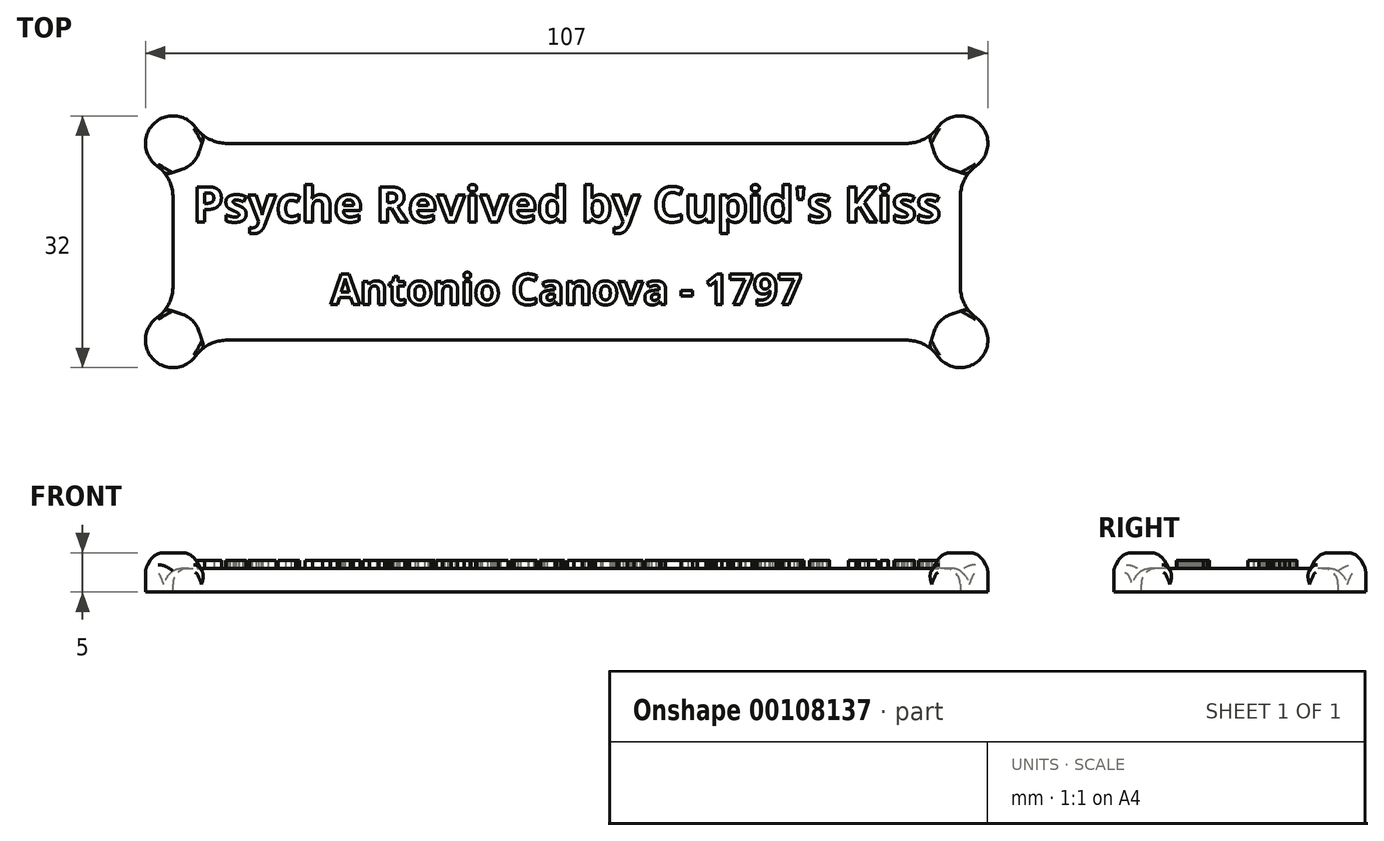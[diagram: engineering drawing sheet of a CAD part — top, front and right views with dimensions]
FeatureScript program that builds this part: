
annotation { "Feature Type Name" : "Feature", "Feature Type Description" : "" }
export const myFeature = defineFeature(function(context is Context, id is Id, definition is map)
    precondition{}
    {
        {
            var Q0;
            Q0=qCreatedBy(makeId("Top.planeOp"),FACE);
            var sketch = newSketch(context, id + "F0", { "sketchPlane" : qUnion([Q0])});
            skLineSegment(sketch, "E0.bottom", {"start": v(50, -12.5) * mm, "end": v(-50, -12.5) * mm});
            skLineSegment(sketch, "E0.top", {"start": v(50, 12.5) * mm, "end": v(-50, 12.5) * mm});
            skLineSegment(sketch, "E0.left", {"start": v(50, -12.5) * mm, "end": v(50, 12.5) * mm});
            skLineSegment(sketch, "E0.right", {"start": v(-50, -12.5) * mm, "end": v(-50, 12.5) * mm});
            skPoint(sketch, "E0.middle", {"position": v(0, 0) * mm});
            skArc(sketch, "E1", {"start": v(-46.5, 12.5) * mm, "mid": v(-52.47, 14.97) * mm, "end": v(-50, 9) * mm});
            skCircle(sketch, "E2", {"center": v(-50, -12.5) * mm, "radius": 3.5 * mm});
            skCircle(sketch, "E3", {"center": v(50, -12.5) * mm, "radius": 3.5 * mm});
            skCircle(sketch, "E4", {"center": v(50, 12.5) * mm, "radius": 3.5 * mm});
            skCircle(sketch, "E5", {"center": v(-50, 12.5) * mm, "radius": 3.5 * mm});
            skSolve(sketch);
        }
        {
            var Q0;
            {var subQ0=sQuery(id+"F0.wireOp",EDGE,"E0.left");var subQ1=sQuery(id+"F0.wireOp",EDGE,"E0.bottom");var subQ2=makeQuery(id+"F0.imprint","INTERSECT",VERTEX,{"derivedFrom":[subQ1,subQ0]});Q0=makeQuery(id+"F0.imprint","IMPRINT",FACE,{"disambiguationData":[TD([[makeQuery(id+"F0.imprint","IMPRINT",EDGE,{"disambiguationData":[TD([[subQ2,-1.0]])],"derivedFrom":subQ1}),1.0]])]});}
            var Q1;
            {var subQ0=sQuery(id+"F0.wireOp",EDGE,"E0.right");var subQ1=sQuery(id+"F0.wireOp",EDGE,"E0.bottom");var subQ2=makeQuery(id+"F0.imprint","INTERSECT",VERTEX,{"derivedFrom":[subQ1,subQ0]});Q1=makeQuery(id+"F0.imprint","IMPRINT",FACE,{"disambiguationData":[TD([[makeQuery(id+"F0.imprint","IMPRINT",EDGE,{"disambiguationData":[TD([[subQ2,1.0]])],"derivedFrom":subQ1}),1.0]])]});}
            var Q2;
            {var subQ0=sQuery(id+"F0.wireOp",EDGE,"E0.left");var subQ1=sQuery(id+"F0.wireOp",EDGE,"E0.top");var subQ2=makeQuery(id+"F0.imprint","INTERSECT",VERTEX,{"derivedFrom":[subQ1,subQ0]});Q2=makeQuery(id+"F0.imprint","IMPRINT",FACE,{"disambiguationData":[TD([[makeQuery(id+"F0.imprint","IMPRINT",EDGE,{"disambiguationData":[TD([[subQ2,-1.0]])],"derivedFrom":subQ1}),-1.0]])]});}
            var Q3;
            {var subQ3=sQuery(id+"F0.wireOp",EDGE,"E1");Q3=makeQuery(id+"F0.imprint","IMPRINT",FACE,{"disambiguationData":[TD([[makeQuery(id+"F0.imprint","IMPRINT",EDGE,{"derivedFrom":subQ3}),1.0]])]});}
            var Q4;
            {var subQ0=sQuery(id+"F0.wireOp",EDGE,"E0.left");var subQ1=sQuery(id+"F0.wireOp",EDGE,"E0.bottom");var subQ2=makeQuery(id+"F0.imprint","INTERSECT",VERTEX,{"derivedFrom":[subQ1,subQ0]});Q4=makeQuery(id+"F0.imprint","IMPRINT",FACE,{"disambiguationData":[TD([[makeQuery(id+"F0.imprint","IMPRINT",EDGE,{"disambiguationData":[TD([[subQ2,-1.0]])],"derivedFrom":subQ1}),-1.0]])]});}
            var Q5;
            {var subQ0=sQuery(id+"F0.wireOp",EDGE,"E0.right");var subQ1=sQuery(id+"F0.wireOp",EDGE,"E0.bottom");var subQ2=makeQuery(id+"F0.imprint","INTERSECT",VERTEX,{"derivedFrom":[subQ1,subQ0]});Q5=makeQuery(id+"F0.imprint","IMPRINT",FACE,{"disambiguationData":[TD([[makeQuery(id+"F0.imprint","IMPRINT",EDGE,{"disambiguationData":[TD([[subQ2,1.0]])],"derivedFrom":subQ1}),-1.0]])]});}
            var Q6;
            {var subQ0=sQuery(id+"F0.wireOp",EDGE,"E0.left");var subQ1=sQuery(id+"F0.wireOp",EDGE,"E0.top");var subQ2=makeQuery(id+"F0.imprint","INTERSECT",VERTEX,{"derivedFrom":[subQ1,subQ0]});Q6=makeQuery(id+"F0.imprint","IMPRINT",FACE,{"disambiguationData":[TD([[makeQuery(id+"F0.imprint","IMPRINT",EDGE,{"disambiguationData":[TD([[subQ2,-1.0]])],"derivedFrom":subQ1}),1.0]])]});}
            var Q7;
            Q7=makeQuery(id+"F0.imprint","IMPRINT",FACE,{"disambiguationData":[TD([[makeQuery(id+"F0.imprint","IMPRINT",EDGE,{"derivedFrom":sQuery(id+"F0.wireOp",EDGE,"687687a7-fea7-4981-826e-90962389b271.sketch_text.stroke-0")}),1.0]])]});
            var Q8;
            Q8 = qSketchRegion(id + "F0", true);
            var Q9;
            Q9=makeQuery(id+"F0.imprint","IMPRINT",FACE,{"disambiguationData":[TD([[makeQuery(id+"F0.imprint","IMPRINT",EDGE,{"derivedFrom":sQuery(id+"F0.wireOp",EDGE,"687687a7-fea7-4981-826e-90962389b271.sketch_text.stroke-211")}),1.0]])]});
            var Q10;
            Q10=makeQuery(id+"F0.imprint","IMPRINT",FACE,{"disambiguationData":[TD([[makeQuery(id+"F0.imprint","IMPRINT",EDGE,{"derivedFrom":sQuery(id+"F0.wireOp",EDGE,"1d88de1f-9107-434d-85d9-702cc254aeca.sketch_text.stroke-49")}),-1.0]])]});
            var Q11;
            Q11=makeQuery(id+"F0.imprint","IMPRINT",FACE,{"disambiguationData":[TD([[makeQuery(id+"F0.imprint","IMPRINT",EDGE,{"derivedFrom":sQuery(id+"F0.wireOp",EDGE,"1d88de1f-9107-434d-85d9-702cc254aeca.sketch_text.stroke-238")}),-1.0]])]});
            var Q12;
            Q12=makeQuery(id+"F0.imprint","IMPRINT",FACE,{"disambiguationData":[TD([[makeQuery(id+"F0.imprint","IMPRINT",EDGE,{"derivedFrom":sQuery(id+"F0.wireOp",EDGE,"1d88de1f-9107-434d-85d9-702cc254aeca.sketch_text.stroke-8")}),1.0]])]});
            var Q13;
            Q13=makeQuery(id+"F0.imprint","IMPRINT",FACE,{"disambiguationData":[TD([[makeQuery(id+"F0.imprint","IMPRINT",EDGE,{"derivedFrom":sQuery(id+"F0.wireOp",EDGE,"687687a7-fea7-4981-826e-90962389b271.sketch_text.stroke-235")}),1.0]])]});
            var Q14;
            Q14=makeQuery(id+"F0.imprint","IMPRINT",FACE,{"disambiguationData":[TD([[makeQuery(id+"F0.imprint","IMPRINT",EDGE,{"derivedFrom":sQuery(id+"F0.wireOp",EDGE,"1d88de1f-9107-434d-85d9-702cc254aeca.sketch_text.stroke-95")}),-1.0]])]});
            var Q15;
            Q15=makeQuery(id+"F0.imprint","IMPRINT",FACE,{"disambiguationData":[TD([[makeQuery(id+"F0.imprint","IMPRINT",EDGE,{"derivedFrom":sQuery(id+"F0.wireOp",EDGE,"1d88de1f-9107-434d-85d9-702cc254aeca.sketch_text.stroke-261")}),1.0]])]});
            var Q16;
            Q16=makeQuery(id+"F0.imprint","IMPRINT",FACE,{"disambiguationData":[TD([[makeQuery(id+"F0.imprint","IMPRINT",EDGE,{"derivedFrom":sQuery(id+"F0.wireOp",EDGE,"1d88de1f-9107-434d-85d9-702cc254aeca.sketch_text.stroke-13")}),-1.0]])]});
            var Q17;
            Q17=makeQuery(id+"F0.imprint","IMPRINT",FACE,{"disambiguationData":[TD([[makeQuery(id+"F0.imprint","IMPRINT",EDGE,{"derivedFrom":sQuery(id+"F0.wireOp",EDGE,"687687a7-fea7-4981-826e-90962389b271.sketch_text.stroke-243")}),-1.0]])]});
            var Q18;
            Q18=makeQuery(id+"F0.imprint","IMPRINT",FACE,{"disambiguationData":[TD([[makeQuery(id+"F0.imprint","IMPRINT",EDGE,{"derivedFrom":sQuery(id+"F0.wireOp",EDGE,"1d88de1f-9107-434d-85d9-702cc254aeca.sketch_text.stroke-127")}),-1.0]])]});
            var Q19;
            Q19=makeQuery(id+"F0.imprint","IMPRINT",FACE,{"disambiguationData":[TD([[makeQuery(id+"F0.imprint","IMPRINT",EDGE,{"derivedFrom":sQuery(id+"F0.wireOp",EDGE,"1d88de1f-9107-434d-85d9-702cc254aeca.sketch_text.stroke-271")}),-1.0]])]});
            var Q20;
            Q20=makeQuery(id+"F0.imprint","IMPRINT",FACE,{"disambiguationData":[TD([[makeQuery(id+"F0.imprint","IMPRINT",EDGE,{"derivedFrom":sQuery(id+"F0.wireOp",EDGE,"1d88de1f-9107-434d-85d9-702cc254aeca.sketch_text.stroke-30")}),-1.0]])]});
            var Q21;
            Q21=makeQuery(id+"F0.imprint","IMPRINT",FACE,{"disambiguationData":[TD([[makeQuery(id+"F0.imprint","IMPRINT",EDGE,{"derivedFrom":sQuery(id+"F0.wireOp",EDGE,"687687a7-fea7-4981-826e-90962389b271.sketch_text.stroke-259")}),-1.0]])]});
            var Q22;
            Q22=makeQuery(id+"F0.imprint","IMPRINT",FACE,{"disambiguationData":[TD([[makeQuery(id+"F0.imprint","IMPRINT",EDGE,{"derivedFrom":sQuery(id+"F0.wireOp",EDGE,"1d88de1f-9107-434d-85d9-702cc254aeca.sketch_text.stroke-171")}),-1.0]])]});
            var Q23;
            Q23=makeQuery(id+"F0.imprint","IMPRINT",FACE,{"disambiguationData":[TD([[makeQuery(id+"F0.imprint","IMPRINT",EDGE,{"derivedFrom":sQuery(id+"F0.wireOp",EDGE,"1d88de1f-9107-434d-85d9-702cc254aeca.sketch_text.stroke-58")}),1.0]])]});
            var Q24;
            Q24=makeQuery(id+"F0.imprint","IMPRINT",FACE,{"disambiguationData":[TD([[makeQuery(id+"F0.imprint","IMPRINT",EDGE,{"derivedFrom":sQuery(id+"F0.wireOp",EDGE,"687687a7-fea7-4981-826e-90962389b271.sketch_text.stroke-274")}),-1.0]])]});
            var Q25;
            Q25=makeQuery(id+"F0.imprint","IMPRINT",FACE,{"disambiguationData":[TD([[makeQuery(id+"F0.imprint","IMPRINT",EDGE,{"derivedFrom":sQuery(id+"F0.wireOp",EDGE,"1d88de1f-9107-434d-85d9-702cc254aeca.sketch_text.stroke-198")}),-1.0]])]});
            var Q26;
            Q26=makeQuery(id+"F0.imprint","IMPRINT",FACE,{"disambiguationData":[TD([[makeQuery(id+"F0.imprint","IMPRINT",EDGE,{"derivedFrom":sQuery(id+"F0.wireOp",EDGE,"1d88de1f-9107-434d-85d9-702cc254aeca.sketch_text.stroke-66")}),-1.0]])]});
            var Q27;
            Q27=makeQuery(id+"F0.imprint","IMPRINT",FACE,{"disambiguationData":[TD([[makeQuery(id+"F0.imprint","IMPRINT",EDGE,{"derivedFrom":sQuery(id+"F0.wireOp",EDGE,"1d88de1f-9107-434d-85d9-702cc254aeca.sketch_text.stroke-245")}),-1.0]])]});
            var Q28;
            Q28=makeQuery(id+"F0.imprint","IMPRINT",FACE,{"disambiguationData":[TD([[makeQuery(id+"F0.imprint","IMPRINT",EDGE,{"derivedFrom":sQuery(id+"F0.wireOp",EDGE,"1d88de1f-9107-434d-85d9-702cc254aeca.sketch_text.stroke-83")}),-1.0]])]});
            var Q29;
            Q29=makeQuery(id+"F0.imprint","IMPRINT",FACE,{"disambiguationData":[TD([[makeQuery(id+"F0.imprint","IMPRINT",EDGE,{"derivedFrom":sQuery(id+"F0.wireOp",EDGE,"687687a7-fea7-4981-826e-90962389b271.sketch_text.stroke-307")}),1.0]])]});
            var Q30;
            Q30=makeQuery(id+"F0.imprint","IMPRINT",FACE,{"disambiguationData":[TD([[makeQuery(id+"F0.imprint","IMPRINT",EDGE,{"derivedFrom":sQuery(id+"F0.wireOp",EDGE,"687687a7-fea7-4981-826e-90962389b271.sketch_text.stroke-0")}),-1.0]])]});
            var Q31;
            Q31=makeQuery(id+"F0.imprint","IMPRINT",FACE,{"disambiguationData":[TD([[makeQuery(id+"F0.imprint","IMPRINT",EDGE,{"derivedFrom":sQuery(id+"F0.wireOp",EDGE,"1d88de1f-9107-434d-85d9-702cc254aeca.sketch_text.stroke-87")}),-1.0]])]});
            var Q32;
            Q32=makeQuery(id+"F0.imprint","IMPRINT",FACE,{"disambiguationData":[TD([[makeQuery(id+"F0.imprint","IMPRINT",EDGE,{"derivedFrom":sQuery(id+"F0.wireOp",EDGE,"687687a7-fea7-4981-826e-90962389b271.sketch_text.stroke-316")}),-1.0]])]});
            var Q33;
            Q33=makeQuery(id+"F0.imprint","IMPRINT",FACE,{"disambiguationData":[TD([[makeQuery(id+"F0.imprint","IMPRINT",EDGE,{"derivedFrom":sQuery(id+"F0.wireOp",EDGE,"687687a7-fea7-4981-826e-90962389b271.sketch_text.stroke-119")}),1.0]])]});
            var Q34;
            Q34=makeQuery(id+"F0.imprint","IMPRINT",FACE,{"disambiguationData":[TD([[makeQuery(id+"F0.imprint","IMPRINT",EDGE,{"derivedFrom":sQuery(id+"F0.wireOp",EDGE,"687687a7-fea7-4981-826e-90962389b271.sketch_text.stroke-89")}),-1.0]])]});
            var Q35;
            Q35=makeQuery(id+"F0.imprint","IMPRINT",FACE,{"disambiguationData":[TD([[makeQuery(id+"F0.imprint","IMPRINT",EDGE,{"derivedFrom":sQuery(id+"F0.wireOp",EDGE,"1d88de1f-9107-434d-85d9-702cc254aeca.sketch_text.stroke-104")}),1.0]])]});
            var Q36;
            Q36=makeQuery(id+"F0.imprint","IMPRINT",FACE,{"disambiguationData":[TD([[makeQuery(id+"F0.imprint","IMPRINT",EDGE,{"derivedFrom":sQuery(id+"F0.wireOp",EDGE,"687687a7-fea7-4981-826e-90962389b271.sketch_text.stroke-140")}),1.0]])]});
            var Q37;
            Q37=makeQuery(id+"F0.imprint","IMPRINT",FACE,{"disambiguationData":[TD([[makeQuery(id+"F0.imprint","IMPRINT",EDGE,{"derivedFrom":sQuery(id+"F0.wireOp",EDGE,"687687a7-fea7-4981-826e-90962389b271.sketch_text.stroke-320")}),-1.0]])]});
            var Q38;
            Q38=makeQuery(id+"F0.imprint","IMPRINT",FACE,{"disambiguationData":[TD([[makeQuery(id+"F0.imprint","IMPRINT",EDGE,{"derivedFrom":sQuery(id+"F0.wireOp",EDGE,"687687a7-fea7-4981-826e-90962389b271.sketch_text.stroke-108")}),-1.0]])]});
            var Q39;
            Q39=makeQuery(id+"F0.imprint","IMPRINT",FACE,{"disambiguationData":[TD([[makeQuery(id+"F0.imprint","IMPRINT",EDGE,{"derivedFrom":sQuery(id+"F0.wireOp",EDGE,"1d88de1f-9107-434d-85d9-702cc254aeca.sketch_text.stroke-112")}),-1.0]])]});
            var Q40;
            Q40=makeQuery(id+"F0.imprint","IMPRINT",FACE,{"disambiguationData":[TD([[makeQuery(id+"F0.imprint","IMPRINT",EDGE,{"derivedFrom":sQuery(id+"F0.wireOp",EDGE,"687687a7-fea7-4981-826e-90962389b271.sketch_text.stroke-145")}),-1.0]])]});
            var Q41;
            Q41=makeQuery(id+"F0.imprint","IMPRINT",FACE,{"disambiguationData":[TD([[makeQuery(id+"F0.imprint","IMPRINT",EDGE,{"derivedFrom":sQuery(id+"F0.wireOp",EDGE,"687687a7-fea7-4981-826e-90962389b271.sketch_text.stroke-343")}),1.0]])]});
            var Q42;
            Q42=makeQuery(id+"F0.imprint","IMPRINT",FACE,{"disambiguationData":[TD([[makeQuery(id+"F0.imprint","IMPRINT",EDGE,{"derivedFrom":sQuery(id+"F0.wireOp",EDGE,"687687a7-fea7-4981-826e-90962389b271.sketch_text.stroke-126")}),-1.0]])]});
            var Q43;
            Q43=makeQuery(id+"F0.imprint","IMPRINT",FACE,{"disambiguationData":[TD([[makeQuery(id+"F0.imprint","IMPRINT",EDGE,{"derivedFrom":sQuery(id+"F0.wireOp",EDGE,"1d88de1f-9107-434d-85d9-702cc254aeca.sketch_text.stroke-146")}),1.0]])]});
            var Q44;
            Q44=makeQuery(id+"F0.imprint","IMPRINT",FACE,{"disambiguationData":[TD([[makeQuery(id+"F0.imprint","IMPRINT",EDGE,{"derivedFrom":sQuery(id+"F0.wireOp",EDGE,"687687a7-fea7-4981-826e-90962389b271.sketch_text.stroke-352")}),-1.0]])]});
            var Q45;
            Q45=makeQuery(id+"F0.imprint","IMPRINT",FACE,{"disambiguationData":[TD([[makeQuery(id+"F0.imprint","IMPRINT",EDGE,{"derivedFrom":sQuery(id+"F0.wireOp",EDGE,"687687a7-fea7-4981-826e-90962389b271.sketch_text.stroke-177")}),-1.0]])]});
            var Q46;
            Q46=makeQuery(id+"F0.imprint","IMPRINT",FACE,{"disambiguationData":[TD([[makeQuery(id+"F0.imprint","IMPRINT",EDGE,{"derivedFrom":sQuery(id+"F0.wireOp",EDGE,"1d88de1f-9107-434d-85d9-702cc254aeca.sketch_text.stroke-154")}),-1.0]])]});
            var Q47;
            Q47=makeQuery(id+"F0.imprint","IMPRINT",FACE,{"disambiguationData":[TD([[makeQuery(id+"F0.imprint","IMPRINT",EDGE,{"derivedFrom":sQuery(id+"F0.wireOp",EDGE,"687687a7-fea7-4981-826e-90962389b271.sketch_text.stroke-356")}),-1.0]])]});
            var Q48;
            Q48=makeQuery(id+"F0.imprint","IMPRINT",FACE,{"disambiguationData":[TD([[makeQuery(id+"F0.imprint","IMPRINT",EDGE,{"derivedFrom":sQuery(id+"F0.wireOp",EDGE,"687687a7-fea7-4981-826e-90962389b271.sketch_text.stroke-196")}),-1.0]])]});
            var Q49;
            Q49=makeQuery(id+"F0.imprint","IMPRINT",FACE,{"disambiguationData":[TD([[makeQuery(id+"F0.imprint","IMPRINT",EDGE,{"derivedFrom":sQuery(id+"F0.wireOp",EDGE,"1d88de1f-9107-434d-85d9-702cc254aeca.sketch_text.stroke-180")}),1.0]])]});
            var Q50;
            Q50=makeQuery(id+"F0.imprint","IMPRINT",FACE,{"disambiguationData":[TD([[makeQuery(id+"F0.imprint","IMPRINT",EDGE,{"derivedFrom":sQuery(id+"F0.wireOp",EDGE,"687687a7-fea7-4981-826e-90962389b271.sketch_text.stroke-381")}),-1.0]])]});
            var Q51;
            Q51=makeQuery(id+"F0.imprint","IMPRINT",FACE,{"disambiguationData":[TD([[makeQuery(id+"F0.imprint","IMPRINT",EDGE,{"derivedFrom":sQuery(id+"F0.wireOp",EDGE,"687687a7-fea7-4981-826e-90962389b271.sketch_text.stroke-167")}),-1.0]])]});
            var Q52;
            Q52=makeQuery(id+"F0.imprint","IMPRINT",FACE,{"disambiguationData":[TD([[makeQuery(id+"F0.imprint","IMPRINT",EDGE,{"derivedFrom":sQuery(id+"F0.wireOp",EDGE,"687687a7-fea7-4981-826e-90962389b271.sketch_text.stroke-155")}),-1.0]])]});
            var Q53;
            Q53=makeQuery(id+"F0.imprint","IMPRINT",FACE,{"disambiguationData":[TD([[makeQuery(id+"F0.imprint","IMPRINT",EDGE,{"derivedFrom":sQuery(id+"F0.wireOp",EDGE,"687687a7-fea7-4981-826e-90962389b271.sketch_text.stroke-159")}),-1.0]])]});
            var Q54;
            Q54=makeQuery(id+"F0.imprint","IMPRINT",FACE,{"disambiguationData":[TD([[makeQuery(id+"F0.imprint","IMPRINT",EDGE,{"derivedFrom":sQuery(id+"F0.wireOp",EDGE,"687687a7-fea7-4981-826e-90962389b271.sketch_text.stroke-8")}),1.0]])]});
            var Q55;
            Q55=makeQuery(id+"F0.imprint","IMPRINT",FACE,{"disambiguationData":[TD([[makeQuery(id+"F0.imprint","IMPRINT",EDGE,{"derivedFrom":sQuery(id+"F0.wireOp",EDGE,"687687a7-fea7-4981-826e-90962389b271.sketch_text.stroke-15")}),-1.0]])]});
            var Q56;
            Q56=makeQuery(id+"F0.imprint","IMPRINT",FACE,{"disambiguationData":[TD([[makeQuery(id+"F0.imprint","IMPRINT",EDGE,{"derivedFrom":sQuery(id+"F0.wireOp",EDGE,"687687a7-fea7-4981-826e-90962389b271.sketch_text.stroke-40")}),-1.0]])]});
            var Q57;
            Q57=makeQuery(id+"F0.imprint","IMPRINT",FACE,{"disambiguationData":[TD([[makeQuery(id+"F0.imprint","IMPRINT",EDGE,{"derivedFrom":sQuery(id+"F0.wireOp",EDGE,"687687a7-fea7-4981-826e-90962389b271.sketch_text.stroke-56")}),-1.0]])]});
            var Q58;
            Q58=makeQuery(id+"F0.imprint","IMPRINT",FACE,{"disambiguationData":[TD([[makeQuery(id+"F0.imprint","IMPRINT",EDGE,{"derivedFrom":sQuery(id+"F0.wireOp",EDGE,"687687a7-fea7-4981-826e-90962389b271.sketch_text.stroke-71")}),-1.0]])]});
            var Q59;
            Q59=makeQuery(id+"F0.imprint","IMPRINT",FACE,{"disambiguationData":[TD([[makeQuery(id+"F0.imprint","IMPRINT",EDGE,{"derivedFrom":sQuery(id+"F0.wireOp",EDGE,"687687a7-fea7-4981-826e-90962389b271.sketch_text.stroke-103")}),1.0]])]});
            var Q60;
            Q60=makeQuery(id+"F0.imprint","IMPRINT",FACE,{"disambiguationData":[TD([[makeQuery(id+"F0.imprint","IMPRINT",EDGE,{"derivedFrom":sQuery(id+"F0.wireOp",EDGE,"687687a7-fea7-4981-826e-90962389b271.sketch_text.stroke-430")}),-1.0]])]});
            var Q61;
            Q61=makeQuery(id+"F0.imprint","IMPRINT",FACE,{"disambiguationData":[TD([[makeQuery(id+"F0.imprint","IMPRINT",EDGE,{"derivedFrom":sQuery(id+"F0.wireOp",EDGE,"1d88de1f-9107-434d-85d9-702cc254aeca.sketch_text.stroke-229")}),-1.0]])]});
            var Q62;
            Q62=makeQuery(id+"F0.imprint","IMPRINT",FACE,{"disambiguationData":[TD([[makeQuery(id+"F0.imprint","IMPRINT",EDGE,{"derivedFrom":sQuery(id+"F0.wireOp",EDGE,"1d88de1f-9107-434d-85d9-702cc254aeca.sketch_text.stroke-0")}),-1.0]])]});
            var Q63;
            Q63=makeQuery(id+"F0.imprint","IMPRINT",FACE,{"disambiguationData":[TD([[makeQuery(id+"F0.imprint","IMPRINT",EDGE,{"derivedFrom":sQuery(id+"F0.wireOp",EDGE,"687687a7-fea7-4981-826e-90962389b271.sketch_text.stroke-191")}),1.0]])]});
            var Q64;
            Q64=makeQuery(id+"F0.imprint","IMPRINT",FACE,{"disambiguationData":[TD([[makeQuery(id+"F0.imprint","IMPRINT",EDGE,{"derivedFrom":sQuery(id+"F0.wireOp",EDGE,"687687a7-fea7-4981-826e-90962389b271.sketch_text.stroke-397")}),-1.0]])]});
            var Q65;
            Q65=makeQuery(id+"F0.imprint","IMPRINT",FACE,{"disambiguationData":[TD([[makeQuery(id+"F0.imprint","IMPRINT",EDGE,{"derivedFrom":sQuery(id+"F0.wireOp",EDGE,"1d88de1f-9107-434d-85d9-702cc254aeca.sketch_text.stroke-217")}),1.0]])]});
            var Q66;
            Q66=makeQuery(id+"F0.imprint","IMPRINT",FACE,{"disambiguationData":[TD([[makeQuery(id+"F0.imprint","IMPRINT",EDGE,{"derivedFrom":sQuery(id+"F0.wireOp",EDGE,"687687a7-fea7-4981-826e-90962389b271.sketch_text.stroke-291")}),-1.0]])]});
            var Q67;
            Q67=makeQuery(id+"F0.imprint","IMPRINT",FACE,{"disambiguationData":[TD([[makeQuery(id+"F0.imprint","IMPRINT",EDGE,{"derivedFrom":sQuery(id+"F0.wireOp",EDGE,"687687a7-fea7-4981-826e-90962389b271.sketch_text.stroke-393")}),-1.0]])]});
            var Q68;
            Q68=makeQuery(id+"F0.imprint","IMPRINT",FACE,{"disambiguationData":[TD([[makeQuery(id+"F0.imprint","IMPRINT",EDGE,{"derivedFrom":sQuery(id+"F0.wireOp",EDGE,"1d88de1f-9107-434d-85d9-702cc254aeca.sketch_text.stroke-188")}),-1.0]])]});
            var Q69;
            Q69=makeQuery(id+"F0.imprint","IMPRINT",FACE,{"disambiguationData":[TD([[makeQuery(id+"F0.imprint","IMPRINT",EDGE,{"derivedFrom":sQuery(id+"F0.wireOp",EDGE,"687687a7-fea7-4981-826e-90962389b271.sketch_text.stroke-220")}),-1.0]])]});
            var Q70;
            Q70=makeQuery(id+"F0.imprint","IMPRINT",FACE,{"disambiguationData":[TD([[makeQuery(id+"F0.imprint","IMPRINT",EDGE,{"derivedFrom":sQuery(id+"F0.wireOp",EDGE,"1d88de1f-9107-434d-85d9-702cc254aeca.sketch_text.stroke-225")}),-1.0]])]});
            var Q71;
            Q71=makeQuery(id+"F0.imprint","IMPRINT",FACE,{"disambiguationData":[TD([[makeQuery(id+"F0.imprint","IMPRINT",EDGE,{"derivedFrom":sQuery(id+"F0.wireOp",EDGE,"687687a7-fea7-4981-826e-90962389b271.sketch_text.stroke-328")}),-1.0]])]});
            var Q72;
            Q72=makeQuery(id+"F0.imprint","IMPRINT",FACE,{"disambiguationData":[TD([[makeQuery(id+"F0.imprint","IMPRINT",EDGE,{"derivedFrom":sQuery(id+"F0.wireOp",EDGE,"687687a7-fea7-4981-826e-90962389b271.sketch_text.stroke-405")}),-1.0]])]});
            extrude(context, id + "F1", {"entities" : qUnion([Q0, Q1, Q2, Q3, Q4, Q5, Q6, Q7, Q8, Q9, Q10, Q11, Q12, Q13, Q14, Q15, Q16, Q17, Q18, Q19, Q20, Q21, Q22, Q23, Q24, Q25, Q26, Q27, Q28, Q29, Q30, Q31, Q32, Q33, Q34, Q35, Q36, Q37, Q38, Q39, Q40, Q41, Q42, Q43, Q44, Q45, Q46, Q47, Q48, Q49, Q50, Q51, Q52, Q53, Q54, Q55, Q56, Q57, Q58, Q59, Q60, Q61, Q62, Q63, Q64, Q65, Q66, Q67, Q68, Q69, Q70, Q71, Q72]), "oppositeDirection" : true, "depth" : 3 * mm});
        }
        {
            var Q0;
            Q0=makeQuery(id+"F1.opExtrude","CAP_FACE",FACE,{"disambiguationData":[OSD([sQuery(id+"F0.wireOp",EDGE,"E0.bottom"),sQuery(id+"F0.wireOp",EDGE,"E0.top"),sQuery(id+"F0.wireOp",EDGE,"E0.left"),sQuery(id+"F0.wireOp",EDGE,"E0.right"),sQuery(id+"F0.wireOp",EDGE,"E1"),sQuery(id+"F0.wireOp",EDGE,"E2"),sQuery(id+"F0.wireOp",EDGE,"E3"),sQuery(id+"F0.wireOp",EDGE,"E4")])],"isStart":true});
            var sketch = newSketch(context, id + "F2", { "sketchPlane" : qUnion([Q0])});
            skText(sketch, "E6", { "text": "Psyche Revived by Cupid\'s Kiss", "fontName": "OpenSans-Bold.ttf"});
            skText(sketch, "E7", { "text": "Antonio Canova - 1797", "fontName": "OpenSans-Bold.ttf"});
            const initialGuessF2  = {"E6": [-0.0475, 0.00252, 1, 0, 0.0045], "E7": [-0.03, -0.00798, 1, 0, 0.0039]};
            skSetInitialGuess(sketch, initialGuessF2);
            skSolve(sketch);
        }
        {
            var Q0;
            Q0 = qSketchRegion(id + "F2", true);
            extrude(context, id + "F3", {"entities" : qUnion([Q0]), "operationType" : NewBodyOperationType.ADD, "depth" : 1 * mm});
        }
        {
            var Q0;
            {var subQ0=sQuery(id+"F0.wireOp",EDGE,"E0.right");var subQ1=sQuery(id+"F0.wireOp",EDGE,"E0.top");var subQ2=makeQuery(id+"F0.imprint","INTERSECT",VERTEX,{"derivedFrom":[subQ1,subQ0]});Q0=makeQuery(id+"F0.imprint","IMPRINT",FACE,{"disambiguationData":[TD([[makeQuery(id+"F0.imprint","IMPRINT",EDGE,{"disambiguationData":[TD([[subQ2,1.0]])],"derivedFrom":subQ1}),-1.0]])]});}
            var Q1;
            {var subQ0=sQuery(id+"F0.wireOp",EDGE,"E0.right");var subQ1=sQuery(id+"F0.wireOp",EDGE,"E0.top");var subQ2=makeQuery(id+"F0.imprint","INTERSECT",VERTEX,{"derivedFrom":[subQ1,subQ0]});Q1=makeQuery(id+"F0.imprint","IMPRINT",FACE,{"disambiguationData":[TD([[makeQuery(id+"F0.imprint","IMPRINT",EDGE,{"disambiguationData":[TD([[subQ2,1.0]])],"derivedFrom":subQ1}),1.0]])]});}
            var Q2;
            {var subQ0=sQuery(id+"F0.wireOp",EDGE,"E0.right");var subQ1=sQuery(id+"F0.wireOp",EDGE,"E0.bottom");var subQ2=makeQuery(id+"F0.imprint","INTERSECT",VERTEX,{"derivedFrom":[subQ1,subQ0]});Q2=makeQuery(id+"F0.imprint","IMPRINT",FACE,{"disambiguationData":[TD([[makeQuery(id+"F0.imprint","IMPRINT",EDGE,{"disambiguationData":[TD([[subQ2,1.0]])],"derivedFrom":subQ1}),1.0]])]});}
            var Q3;
            {var subQ0=sQuery(id+"F0.wireOp",EDGE,"E0.right");var subQ1=sQuery(id+"F0.wireOp",EDGE,"E0.bottom");var subQ2=makeQuery(id+"F0.imprint","INTERSECT",VERTEX,{"derivedFrom":[subQ1,subQ0]});Q3=makeQuery(id+"F0.imprint","IMPRINT",FACE,{"disambiguationData":[TD([[makeQuery(id+"F0.imprint","IMPRINT",EDGE,{"disambiguationData":[TD([[subQ2,1.0]])],"derivedFrom":subQ1}),-1.0]])]});}
            var Q4;
            {var subQ0=sQuery(id+"F0.wireOp",EDGE,"E0.left");var subQ1=sQuery(id+"F0.wireOp",EDGE,"E0.bottom");var subQ2=makeQuery(id+"F0.imprint","INTERSECT",VERTEX,{"derivedFrom":[subQ1,subQ0]});Q4=makeQuery(id+"F0.imprint","IMPRINT",FACE,{"disambiguationData":[TD([[makeQuery(id+"F0.imprint","IMPRINT",EDGE,{"disambiguationData":[TD([[subQ2,-1.0]])],"derivedFrom":subQ1}),1.0]])]});}
            var Q5;
            {var subQ0=sQuery(id+"F0.wireOp",EDGE,"E0.left");var subQ1=sQuery(id+"F0.wireOp",EDGE,"E0.bottom");var subQ2=makeQuery(id+"F0.imprint","INTERSECT",VERTEX,{"derivedFrom":[subQ1,subQ0]});Q5=makeQuery(id+"F0.imprint","IMPRINT",FACE,{"disambiguationData":[TD([[makeQuery(id+"F0.imprint","IMPRINT",EDGE,{"disambiguationData":[TD([[subQ2,-1.0]])],"derivedFrom":subQ1}),-1.0]])]});}
            var Q6;
            {var subQ0=sQuery(id+"F0.wireOp",EDGE,"E0.left");var subQ1=sQuery(id+"F0.wireOp",EDGE,"E0.top");var subQ2=makeQuery(id+"F0.imprint","INTERSECT",VERTEX,{"derivedFrom":[subQ1,subQ0]});Q6=makeQuery(id+"F0.imprint","IMPRINT",FACE,{"disambiguationData":[TD([[makeQuery(id+"F0.imprint","IMPRINT",EDGE,{"disambiguationData":[TD([[subQ2,-1.0]])],"derivedFrom":subQ1}),-1.0]])]});}
            var Q7;
            {var subQ0=sQuery(id+"F0.wireOp",EDGE,"E0.left");var subQ1=sQuery(id+"F0.wireOp",EDGE,"E0.top");var subQ2=makeQuery(id+"F0.imprint","INTERSECT",VERTEX,{"derivedFrom":[subQ1,subQ0]});Q7=makeQuery(id+"F0.imprint","IMPRINT",FACE,{"disambiguationData":[TD([[makeQuery(id+"F0.imprint","IMPRINT",EDGE,{"disambiguationData":[TD([[subQ2,-1.0]])],"derivedFrom":subQ1}),1.0]])]});}
            extrude(context, id + "F4", {"entities" : qUnion([Q0, Q1, Q2, Q3, Q4, Q5, Q6, Q7]), "operationType" : NewBodyOperationType.ADD, "depth" : 2 * mm, "hasDraft" : true, "draftAngle" : 30 * degree, "draftPullDirection" : true});
        }
        {
            var Q0;
            Q0=makeQuery(id+"F1.opExtrude","SWEPT_EDGE",EDGE,{"disambiguationData":[OSD([sQuery(id+"F0.wireOp",EDGE,"E0.bottom"),sQuery(id+"F0.wireOp",EDGE,"E2")])]});
            var Q1;
            Q1=makeQuery(id+"F1.opExtrude","SWEPT_EDGE",EDGE,{"disambiguationData":[OSD([sQuery(id+"F0.wireOp",EDGE,"E0.right"),sQuery(id+"F0.wireOp",EDGE,"E2")])]});
            var Q2;
            Q2=makeQuery(id+"F1.opExtrude","SWEPT_EDGE",EDGE,{"disambiguationData":[OSD([sQuery(id+"F0.wireOp",EDGE,"E0.right"),sQuery(id+"F0.wireOp",EDGE,"E5")])]});
            var Q3;
            Q3=makeQuery(id+"F1.opExtrude","SWEPT_EDGE",EDGE,{"disambiguationData":[OSD([sQuery(id+"F0.wireOp",EDGE,"E0.top"),sQuery(id+"F0.wireOp",EDGE,"E5")])]});
            var Q4;
            Q4=makeQuery(id+"F1.opExtrude","SWEPT_EDGE",EDGE,{"disambiguationData":[OSD([sQuery(id+"F0.wireOp",EDGE,"E0.top"),sQuery(id+"F0.wireOp",EDGE,"E4")])]});
            var Q5;
            Q5=makeQuery(id+"F1.opExtrude","SWEPT_EDGE",EDGE,{"disambiguationData":[OSD([sQuery(id+"F0.wireOp",EDGE,"E0.left"),sQuery(id+"F0.wireOp",EDGE,"E4")])]});
            var Q6;
            Q6=makeQuery(id+"F1.opExtrude","SWEPT_EDGE",EDGE,{"disambiguationData":[OSD([sQuery(id+"F0.wireOp",EDGE,"E0.left"),sQuery(id+"F0.wireOp",EDGE,"E3")])]});
            var Q7;
            Q7=makeQuery(id+"F1.opExtrude","SWEPT_EDGE",EDGE,{"disambiguationData":[OSD([sQuery(id+"F0.wireOp",EDGE,"E0.bottom"),sQuery(id+"F0.wireOp",EDGE,"E3")])]});
            fillet(context, id + "F5", {"entities" : qUnion([Q0, Q1, Q2, Q3, Q4, Q5, Q6, Q7]), "radius" : 5 * mm, "tangentPropagation" : true, "allowEdgeOverflow" : false});
        }
        {
            var Q0;
            Q0=makeQuery(id+"F1.opExtrude","CAP_EDGE",EDGE,{"disambiguationData":[OSD([sQuery(id+"F0.wireOp",EDGE,"E0.bottom")])],"isStart":true});
            var Q1;
            {var subQ0=sQuery(id+"F0.wireOp",EDGE,"E2");Q1=makeQuery(id+"F4.boolean.opBoolean","MERGE",EDGE,{"derivedFrom":[makeQuery(id+"F1.opExtrude","CAP_EDGE",EDGE,{"disambiguationData":[OSD([subQ0])],"isStart":true}),makeQuery(id+"F4.opExtrude","CAP_EDGE",EDGE,{"disambiguationData":[OSD([subQ0])],"isStart":true})]});}
            var Q2;
            Q2=makeQuery(id+"F1.opExtrude","CAP_EDGE",EDGE,{"disambiguationData":[OSD([sQuery(id+"F0.wireOp",EDGE,"E0.right")])],"isStart":true});
            var Q3;
            {var subQ0=sQuery(id+"F0.wireOp",EDGE,"E5");Q3=makeQuery(id+"F4.boolean.opBoolean","MERGE",EDGE,{"derivedFrom":[makeQuery(id+"F1.opExtrude","CAP_EDGE",EDGE,{"disambiguationData":[OSD([subQ0])],"isStart":true}),makeQuery(id+"F4.opExtrude","CAP_EDGE",EDGE,{"disambiguationData":[OSD([subQ0])],"isStart":true})]});}
            var Q4;
            Q4=makeQuery(id+"F1.opExtrude","CAP_EDGE",EDGE,{"disambiguationData":[OSD([sQuery(id+"F0.wireOp",EDGE,"E0.top")])],"isStart":true});
            var Q5;
            {var subQ0=sQuery(id+"F0.wireOp",EDGE,"E4");Q5=makeQuery(id+"F4.boolean.opBoolean","MERGE",EDGE,{"derivedFrom":[makeQuery(id+"F1.opExtrude","CAP_EDGE",EDGE,{"disambiguationData":[OSD([subQ0])],"isStart":true}),makeQuery(id+"F4.opExtrude","CAP_EDGE",EDGE,{"disambiguationData":[OSD([subQ0])],"isStart":true})]});}
            var Q6;
            Q6=makeQuery(id+"F1.opExtrude","CAP_EDGE",EDGE,{"disambiguationData":[OSD([sQuery(id+"F0.wireOp",EDGE,"E0.left")])],"isStart":true});
            var Q7;
            {var subQ0=sQuery(id+"F0.wireOp",EDGE,"E3");Q7=makeQuery(id+"F4.boolean.opBoolean","MERGE",EDGE,{"derivedFrom":[makeQuery(id+"F1.opExtrude","CAP_EDGE",EDGE,{"disambiguationData":[OSD([subQ0])],"isStart":true}),makeQuery(id+"F4.opExtrude","CAP_EDGE",EDGE,{"disambiguationData":[OSD([subQ0])],"isStart":true})]});}
            var Q8;
            {var subQ0=sQuery(id+"F0.wireOp",EDGE,"E0.top");var subQ1=sQuery(id+"F0.wireOp",EDGE,"E3");var subQ2=sQuery(id+"F0.wireOp",EDGE,"E4");var subQ3=sQuery(id+"F0.wireOp",EDGE,"E5");var subQ4=sQuery(id+"F0.wireOp",EDGE,"E0.left");var subQ5=sQuery(id+"F0.wireOp",EDGE,"E0.bottom");var subQ6=sQuery(id+"F0.wireOp",EDGE,"E0.right");var subQ7=sQuery(id+"F0.wireOp",EDGE,"E2");Q8=makeQuery(id+"F5.opFillet","BLEND_EDGE",EDGE,{"blendedFrom":[makeQuery(id+"F1.opExtrude","SWEPT_EDGE",EDGE,{"disambiguationData":[OSD([subQ5,subQ7])]}),makeQuery(id+"F3.boolean.opBoolean","SPLIT",FACE,{"disambiguationData":[TD([makeQuery(id+"F1.opExtrude","SWEPT_FACE",FACE,{"disambiguationData":[OSD([subQ5])]})])],"derivedFrom":makeQuery(id+"F1.opExtrude","CAP_FACE",FACE,{"disambiguationData":[OSD([subQ5,subQ0,subQ4,subQ6,subQ7,subQ1,subQ2,subQ3])],"isStart":true})})],"blendedInto":[makeQuery(id+"F3.boolean.opBoolean","SPLIT",FACE,{"disambiguationData":[TD([makeQuery(id+"F1.opExtrude","SWEPT_FACE",FACE,{"disambiguationData":[OSD([subQ5])]})])],"derivedFrom":makeQuery(id+"F1.opExtrude","CAP_FACE",FACE,{"disambiguationData":[OSD([subQ5,subQ0,subQ4,subQ6,subQ7,subQ1,subQ2,subQ3])],"isStart":true})})]});}
            var Q9;
            {var subQ0=sQuery(id+"F0.wireOp",EDGE,"E0.top");var subQ1=sQuery(id+"F0.wireOp",EDGE,"E3");var subQ2=sQuery(id+"F0.wireOp",EDGE,"E4");var subQ3=sQuery(id+"F0.wireOp",EDGE,"E5");var subQ4=sQuery(id+"F0.wireOp",EDGE,"E0.left");var subQ5=sQuery(id+"F0.wireOp",EDGE,"E0.bottom");var subQ6=sQuery(id+"F0.wireOp",EDGE,"E0.right");var subQ7=sQuery(id+"F0.wireOp",EDGE,"E2");Q9=makeQuery(id+"F5.opFillet","BLEND_EDGE",EDGE,{"blendedFrom":[makeQuery(id+"F1.opExtrude","SWEPT_EDGE",EDGE,{"disambiguationData":[OSD([subQ6,subQ7])]}),makeQuery(id+"F3.boolean.opBoolean","SPLIT",FACE,{"disambiguationData":[TD([makeQuery(id+"F1.opExtrude","SWEPT_FACE",FACE,{"disambiguationData":[OSD([subQ5])]})])],"derivedFrom":makeQuery(id+"F1.opExtrude","CAP_FACE",FACE,{"disambiguationData":[OSD([subQ5,subQ0,subQ4,subQ6,subQ7,subQ1,subQ2,subQ3])],"isStart":true})})],"blendedInto":[makeQuery(id+"F3.boolean.opBoolean","SPLIT",FACE,{"disambiguationData":[TD([makeQuery(id+"F1.opExtrude","SWEPT_FACE",FACE,{"disambiguationData":[OSD([subQ5])]})])],"derivedFrom":makeQuery(id+"F1.opExtrude","CAP_FACE",FACE,{"disambiguationData":[OSD([subQ5,subQ0,subQ4,subQ6,subQ7,subQ1,subQ2,subQ3])],"isStart":true})})]});}
            var Q10;
            {var subQ0=sQuery(id+"F0.wireOp",EDGE,"E0.top");var subQ1=sQuery(id+"F0.wireOp",EDGE,"E3");var subQ2=sQuery(id+"F0.wireOp",EDGE,"E4");var subQ3=sQuery(id+"F0.wireOp",EDGE,"E5");var subQ4=sQuery(id+"F0.wireOp",EDGE,"E0.left");var subQ5=sQuery(id+"F0.wireOp",EDGE,"E0.bottom");var subQ6=sQuery(id+"F0.wireOp",EDGE,"E0.right");var subQ7=sQuery(id+"F0.wireOp",EDGE,"E2");Q10=makeQuery(id+"F5.opFillet","BLEND_EDGE",EDGE,{"blendedFrom":[makeQuery(id+"F1.opExtrude","SWEPT_EDGE",EDGE,{"disambiguationData":[OSD([subQ6,subQ3])]}),makeQuery(id+"F3.boolean.opBoolean","SPLIT",FACE,{"disambiguationData":[TD([makeQuery(id+"F1.opExtrude","SWEPT_FACE",FACE,{"disambiguationData":[OSD([subQ5])]})])],"derivedFrom":makeQuery(id+"F1.opExtrude","CAP_FACE",FACE,{"disambiguationData":[OSD([subQ5,subQ0,subQ4,subQ6,subQ7,subQ1,subQ2,subQ3])],"isStart":true})})],"blendedInto":[makeQuery(id+"F3.boolean.opBoolean","SPLIT",FACE,{"disambiguationData":[TD([makeQuery(id+"F1.opExtrude","SWEPT_FACE",FACE,{"disambiguationData":[OSD([subQ5])]})])],"derivedFrom":makeQuery(id+"F1.opExtrude","CAP_FACE",FACE,{"disambiguationData":[OSD([subQ5,subQ0,subQ4,subQ6,subQ7,subQ1,subQ2,subQ3])],"isStart":true})})]});}
            var Q11;
            {var subQ0=sQuery(id+"F0.wireOp",EDGE,"E0.top");var subQ1=sQuery(id+"F0.wireOp",EDGE,"E3");var subQ2=sQuery(id+"F0.wireOp",EDGE,"E4");var subQ3=sQuery(id+"F0.wireOp",EDGE,"E5");var subQ4=sQuery(id+"F0.wireOp",EDGE,"E0.left");var subQ5=sQuery(id+"F0.wireOp",EDGE,"E0.bottom");var subQ6=sQuery(id+"F0.wireOp",EDGE,"E0.right");var subQ7=sQuery(id+"F0.wireOp",EDGE,"E2");Q11=makeQuery(id+"F5.opFillet","BLEND_EDGE",EDGE,{"blendedFrom":[makeQuery(id+"F1.opExtrude","SWEPT_EDGE",EDGE,{"disambiguationData":[OSD([subQ0,subQ3])]}),makeQuery(id+"F3.boolean.opBoolean","SPLIT",FACE,{"disambiguationData":[TD([makeQuery(id+"F1.opExtrude","SWEPT_FACE",FACE,{"disambiguationData":[OSD([subQ5])]})])],"derivedFrom":makeQuery(id+"F1.opExtrude","CAP_FACE",FACE,{"disambiguationData":[OSD([subQ5,subQ0,subQ4,subQ6,subQ7,subQ1,subQ2,subQ3])],"isStart":true})})],"blendedInto":[makeQuery(id+"F3.boolean.opBoolean","SPLIT",FACE,{"disambiguationData":[TD([makeQuery(id+"F1.opExtrude","SWEPT_FACE",FACE,{"disambiguationData":[OSD([subQ5])]})])],"derivedFrom":makeQuery(id+"F1.opExtrude","CAP_FACE",FACE,{"disambiguationData":[OSD([subQ5,subQ0,subQ4,subQ6,subQ7,subQ1,subQ2,subQ3])],"isStart":true})})]});}
            var Q12;
            {var subQ0=sQuery(id+"F0.wireOp",EDGE,"E0.top");var subQ1=sQuery(id+"F0.wireOp",EDGE,"E3");var subQ2=sQuery(id+"F0.wireOp",EDGE,"E4");var subQ3=sQuery(id+"F0.wireOp",EDGE,"E5");var subQ4=sQuery(id+"F0.wireOp",EDGE,"E0.left");var subQ5=sQuery(id+"F0.wireOp",EDGE,"E0.bottom");var subQ6=sQuery(id+"F0.wireOp",EDGE,"E0.right");var subQ7=sQuery(id+"F0.wireOp",EDGE,"E2");Q12=makeQuery(id+"F5.opFillet","BLEND_EDGE",EDGE,{"blendedFrom":[makeQuery(id+"F1.opExtrude","SWEPT_EDGE",EDGE,{"disambiguationData":[OSD([subQ0,subQ2])]}),makeQuery(id+"F3.boolean.opBoolean","SPLIT",FACE,{"disambiguationData":[TD([makeQuery(id+"F1.opExtrude","SWEPT_FACE",FACE,{"disambiguationData":[OSD([subQ5])]})])],"derivedFrom":makeQuery(id+"F1.opExtrude","CAP_FACE",FACE,{"disambiguationData":[OSD([subQ5,subQ0,subQ4,subQ6,subQ7,subQ1,subQ2,subQ3])],"isStart":true})})],"blendedInto":[makeQuery(id+"F3.boolean.opBoolean","SPLIT",FACE,{"disambiguationData":[TD([makeQuery(id+"F1.opExtrude","SWEPT_FACE",FACE,{"disambiguationData":[OSD([subQ5])]})])],"derivedFrom":makeQuery(id+"F1.opExtrude","CAP_FACE",FACE,{"disambiguationData":[OSD([subQ5,subQ0,subQ4,subQ6,subQ7,subQ1,subQ2,subQ3])],"isStart":true})})]});}
            var Q13;
            {var subQ0=sQuery(id+"F0.wireOp",EDGE,"E0.top");var subQ1=sQuery(id+"F0.wireOp",EDGE,"E3");var subQ2=sQuery(id+"F0.wireOp",EDGE,"E4");var subQ3=sQuery(id+"F0.wireOp",EDGE,"E5");var subQ4=sQuery(id+"F0.wireOp",EDGE,"E0.left");var subQ5=sQuery(id+"F0.wireOp",EDGE,"E0.bottom");var subQ6=sQuery(id+"F0.wireOp",EDGE,"E0.right");var subQ7=sQuery(id+"F0.wireOp",EDGE,"E2");Q13=makeQuery(id+"F5.opFillet","BLEND_EDGE",EDGE,{"blendedFrom":[makeQuery(id+"F1.opExtrude","SWEPT_EDGE",EDGE,{"disambiguationData":[OSD([subQ4,subQ2])]}),makeQuery(id+"F3.boolean.opBoolean","SPLIT",FACE,{"disambiguationData":[TD([makeQuery(id+"F1.opExtrude","SWEPT_FACE",FACE,{"disambiguationData":[OSD([subQ5])]})])],"derivedFrom":makeQuery(id+"F1.opExtrude","CAP_FACE",FACE,{"disambiguationData":[OSD([subQ5,subQ0,subQ4,subQ6,subQ7,subQ1,subQ2,subQ3])],"isStart":true})})],"blendedInto":[makeQuery(id+"F3.boolean.opBoolean","SPLIT",FACE,{"disambiguationData":[TD([makeQuery(id+"F1.opExtrude","SWEPT_FACE",FACE,{"disambiguationData":[OSD([subQ5])]})])],"derivedFrom":makeQuery(id+"F1.opExtrude","CAP_FACE",FACE,{"disambiguationData":[OSD([subQ5,subQ0,subQ4,subQ6,subQ7,subQ1,subQ2,subQ3])],"isStart":true})})]});}
            var Q14;
            {var subQ0=sQuery(id+"F0.wireOp",EDGE,"E0.top");var subQ1=sQuery(id+"F0.wireOp",EDGE,"E3");var subQ2=sQuery(id+"F0.wireOp",EDGE,"E4");var subQ3=sQuery(id+"F0.wireOp",EDGE,"E5");var subQ4=sQuery(id+"F0.wireOp",EDGE,"E0.left");var subQ5=sQuery(id+"F0.wireOp",EDGE,"E0.bottom");var subQ6=sQuery(id+"F0.wireOp",EDGE,"E0.right");var subQ7=sQuery(id+"F0.wireOp",EDGE,"E2");Q14=makeQuery(id+"F5.opFillet","BLEND_EDGE",EDGE,{"blendedFrom":[makeQuery(id+"F1.opExtrude","SWEPT_EDGE",EDGE,{"disambiguationData":[OSD([subQ4,subQ1])]}),makeQuery(id+"F3.boolean.opBoolean","SPLIT",FACE,{"disambiguationData":[TD([makeQuery(id+"F1.opExtrude","SWEPT_FACE",FACE,{"disambiguationData":[OSD([subQ5])]})])],"derivedFrom":makeQuery(id+"F1.opExtrude","CAP_FACE",FACE,{"disambiguationData":[OSD([subQ5,subQ0,subQ4,subQ6,subQ7,subQ1,subQ2,subQ3])],"isStart":true})})],"blendedInto":[makeQuery(id+"F3.boolean.opBoolean","SPLIT",FACE,{"disambiguationData":[TD([makeQuery(id+"F1.opExtrude","SWEPT_FACE",FACE,{"disambiguationData":[OSD([subQ5])]})])],"derivedFrom":makeQuery(id+"F1.opExtrude","CAP_FACE",FACE,{"disambiguationData":[OSD([subQ5,subQ0,subQ4,subQ6,subQ7,subQ1,subQ2,subQ3])],"isStart":true})})]});}
            var Q15;
            {var subQ0=sQuery(id+"F0.wireOp",EDGE,"E0.top");var subQ1=sQuery(id+"F0.wireOp",EDGE,"E3");var subQ2=sQuery(id+"F0.wireOp",EDGE,"E4");var subQ3=sQuery(id+"F0.wireOp",EDGE,"E5");var subQ4=sQuery(id+"F0.wireOp",EDGE,"E0.left");var subQ5=sQuery(id+"F0.wireOp",EDGE,"E0.bottom");var subQ6=sQuery(id+"F0.wireOp",EDGE,"E0.right");var subQ7=sQuery(id+"F0.wireOp",EDGE,"E2");Q15=makeQuery(id+"F5.opFillet","BLEND_EDGE",EDGE,{"blendedFrom":[makeQuery(id+"F1.opExtrude","SWEPT_EDGE",EDGE,{"disambiguationData":[OSD([subQ5,subQ1])]}),makeQuery(id+"F3.boolean.opBoolean","SPLIT",FACE,{"disambiguationData":[TD([makeQuery(id+"F1.opExtrude","SWEPT_FACE",FACE,{"disambiguationData":[OSD([subQ5])]})])],"derivedFrom":makeQuery(id+"F1.opExtrude","CAP_FACE",FACE,{"disambiguationData":[OSD([subQ5,subQ0,subQ4,subQ6,subQ7,subQ1,subQ2,subQ3])],"isStart":true})})],"blendedInto":[makeQuery(id+"F3.boolean.opBoolean","SPLIT",FACE,{"disambiguationData":[TD([makeQuery(id+"F1.opExtrude","SWEPT_FACE",FACE,{"disambiguationData":[OSD([subQ5])]})])],"derivedFrom":makeQuery(id+"F1.opExtrude","CAP_FACE",FACE,{"disambiguationData":[OSD([subQ5,subQ0,subQ4,subQ6,subQ7,subQ1,subQ2,subQ3])],"isStart":true})})]});}
            var Q16;
            Q16=makeQuery(id+"F4.opExtrude","CAP_EDGE",EDGE,{"disambiguationData":[OSD([sQuery(id+"F0.wireOp",EDGE,"E2")])],"isStart":false});
            var Q17;
            Q17=makeQuery(id+"F4.opExtrude","CAP_EDGE",EDGE,{"disambiguationData":[OSD([sQuery(id+"F0.wireOp",EDGE,"E5")])],"isStart":false});
            var Q18;
            Q18=makeQuery(id+"F4.opExtrude","CAP_EDGE",EDGE,{"disambiguationData":[OSD([sQuery(id+"F0.wireOp",EDGE,"E4")])],"isStart":false});
            var Q19;
            Q19=makeQuery(id+"F4.opExtrude","CAP_EDGE",EDGE,{"disambiguationData":[OSD([sQuery(id+"F0.wireOp",EDGE,"E3")])],"isStart":false});
            fillet(context, id + "F6", {"entities" : qUnion([Q0, Q1, Q2, Q3, Q4, Q5, Q6, Q7, Q8, Q9, Q10, Q11, Q12, Q13, Q14, Q15, Q16, Q17, Q18, Q19]), "radius" : 2 * mm, "tangentPropagation" : true, "allowEdgeOverflow" : false});
        }
    });
